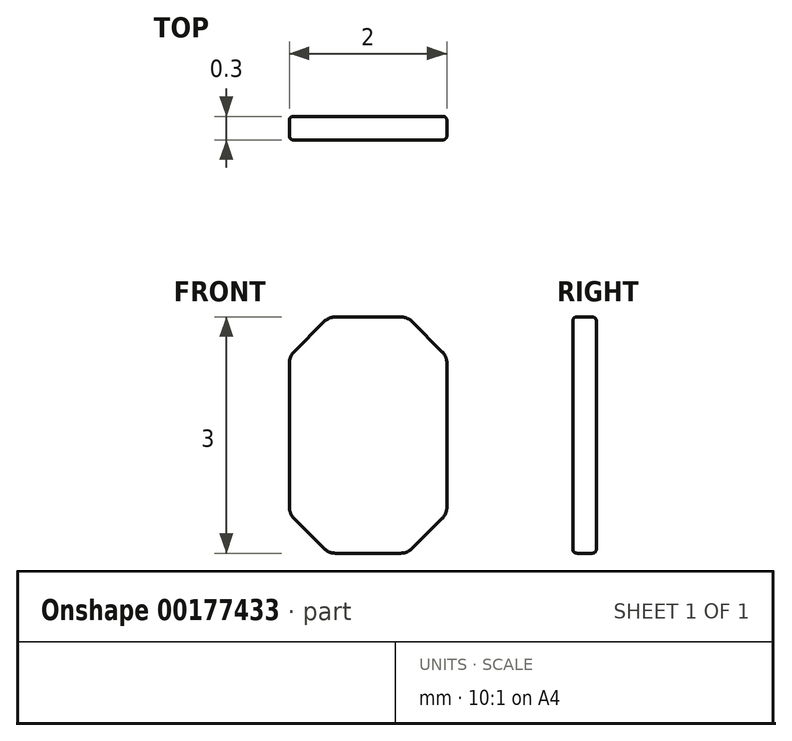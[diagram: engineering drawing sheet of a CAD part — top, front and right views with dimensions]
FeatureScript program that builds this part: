
annotation { "Feature Type Name" : "Feature", "Feature Type Description" : "" }
export const myFeature = defineFeature(function(context is Context, id is Id, definition is map)
    precondition{}
    {
        {
            var Q0;
            Q0=qCreatedBy(makeId("Front.planeOp"),FACE);
            var sketch = newSketch(context, id + "F0", { "sketchPlane" : qUnion([Q0])});
            skLineSegment(sketch, "E0.bottom", {"start": v(0.5, 1.5) * mm, "end": v(-0.5, 1.5) * mm});
            skLineSegment(sketch, "E0.top", {"start": v(0.5, -1.5) * mm, "end": v(-0.5, -1.5) * mm});
            skLineSegment(sketch, "E0.left", {"start": v(0.5, 1.5) * mm, "end": v(0.5, -1.5) * mm});
            skLineSegment(sketch, "E0.right", {"start": v(-0.5, 1.5) * mm, "end": v(-0.5, -1.5) * mm});
            skPoint(sketch, "E0.middle", {"position": v(0, 0) * mm});
            skLineSegment(sketch, "E1", {"start": v(0.5, 1.5) * mm, "end": v(1, 1) * mm});
            skLineSegment(sketch, "E2", {"start": v(1, 1) * mm, "end": v(1, -1) * mm});
            skLineSegment(sketch, "E3", {"start": v(1, -1) * mm, "end": v(0.5, -1.5) * mm});
            skLineSegment(sketch, "E4", {"start": v(-0.5, 1.5) * mm, "end": v(-1, 1) * mm});
            skLineSegment(sketch, "E5", {"start": v(-1, 1) * mm, "end": v(-1, -1) * mm});
            skLineSegment(sketch, "E6", {"start": v(-1, -1) * mm, "end": v(-0.5, -1.5) * mm});
            skSolve(sketch);
        }
        {
            var Q0;
            Q0 = qSketchRegion(id + "F0", true);
            extrude(context, id + "F1", {"entities" : qUnion([Q0]), "depth" : 0.3 * mm});
        }
        {
            var Q0;
            Q0=makeQuery(id+"F1.opExtrude","SWEPT_EDGE",EDGE,{"disambiguationData":[OSD([sQuery(id+"F0.wireOp",EDGE,"E0.bottom"),sQuery(id+"F0.wireOp",EDGE,"E0.left"),sQuery(id+"F0.wireOp",EDGE,"E1")])]});
            var Q1;
            Q1=makeQuery(id+"F1.opExtrude","SWEPT_EDGE",EDGE,{"disambiguationData":[OSD([sQuery(id+"F0.wireOp",EDGE,"E1"),sQuery(id+"F0.wireOp",EDGE,"E2")])]});
            var Q2;
            Q2=makeQuery(id+"F1.opExtrude","SWEPT_EDGE",EDGE,{"disambiguationData":[OSD([sQuery(id+"F0.wireOp",EDGE,"E0.bottom"),sQuery(id+"F0.wireOp",EDGE,"E0.right"),sQuery(id+"F0.wireOp",EDGE,"E4")])]});
            var Q3;
            Q3=makeQuery(id+"F1.opExtrude","SWEPT_EDGE",EDGE,{"disambiguationData":[OSD([sQuery(id+"F0.wireOp",EDGE,"E4"),sQuery(id+"F0.wireOp",EDGE,"E5")])]});
            var Q4;
            Q4=makeQuery(id+"F1.opExtrude","SWEPT_EDGE",EDGE,{"disambiguationData":[OSD([sQuery(id+"F0.wireOp",EDGE,"E5"),sQuery(id+"F0.wireOp",EDGE,"E6")])]});
            var Q5;
            Q5=makeQuery(id+"F1.opExtrude","SWEPT_EDGE",EDGE,{"disambiguationData":[OSD([sQuery(id+"F0.wireOp",EDGE,"E0.top"),sQuery(id+"F0.wireOp",EDGE,"E0.right"),sQuery(id+"F0.wireOp",EDGE,"E6")])]});
            var Q6;
            Q6=makeQuery(id+"F1.opExtrude","SWEPT_EDGE",EDGE,{"disambiguationData":[OSD([sQuery(id+"F0.wireOp",EDGE,"E0.top"),sQuery(id+"F0.wireOp",EDGE,"E0.left"),sQuery(id+"F0.wireOp",EDGE,"E3")])]});
            var Q7;
            Q7=makeQuery(id+"F1.opExtrude","SWEPT_EDGE",EDGE,{"disambiguationData":[OSD([sQuery(id+"F0.wireOp",EDGE,"E2"),sQuery(id+"F0.wireOp",EDGE,"E3")])]});
            fillet(context, id + "F2", {"entities" : qUnion([Q0, Q1, Q2, Q3, Q4, Q5, Q6, Q7]), "radius" : 0.2 * mm, "tangentPropagation" : true, "allowEdgeOverflow" : false});
        }
        {
            var Q0;
            Q0=makeQuery(id+"F1.opExtrude","CAP_EDGE",EDGE,{"disambiguationData":[OSD([sQuery(id+"F0.wireOp",EDGE,"E2")])],"isStart":true});
            var Q1;
            Q1=makeQuery(id+"F1.opExtrude","CAP_EDGE",EDGE,{"disambiguationData":[OSD([sQuery(id+"F0.wireOp",EDGE,"E5")])],"isStart":false});
            fillet(context, id + "F3", {"entities" : qUnion([Q0, Q1]), "radius" : 0.05 * mm, "tangentPropagation" : true, "allowEdgeOverflow" : false});
        }
    });
